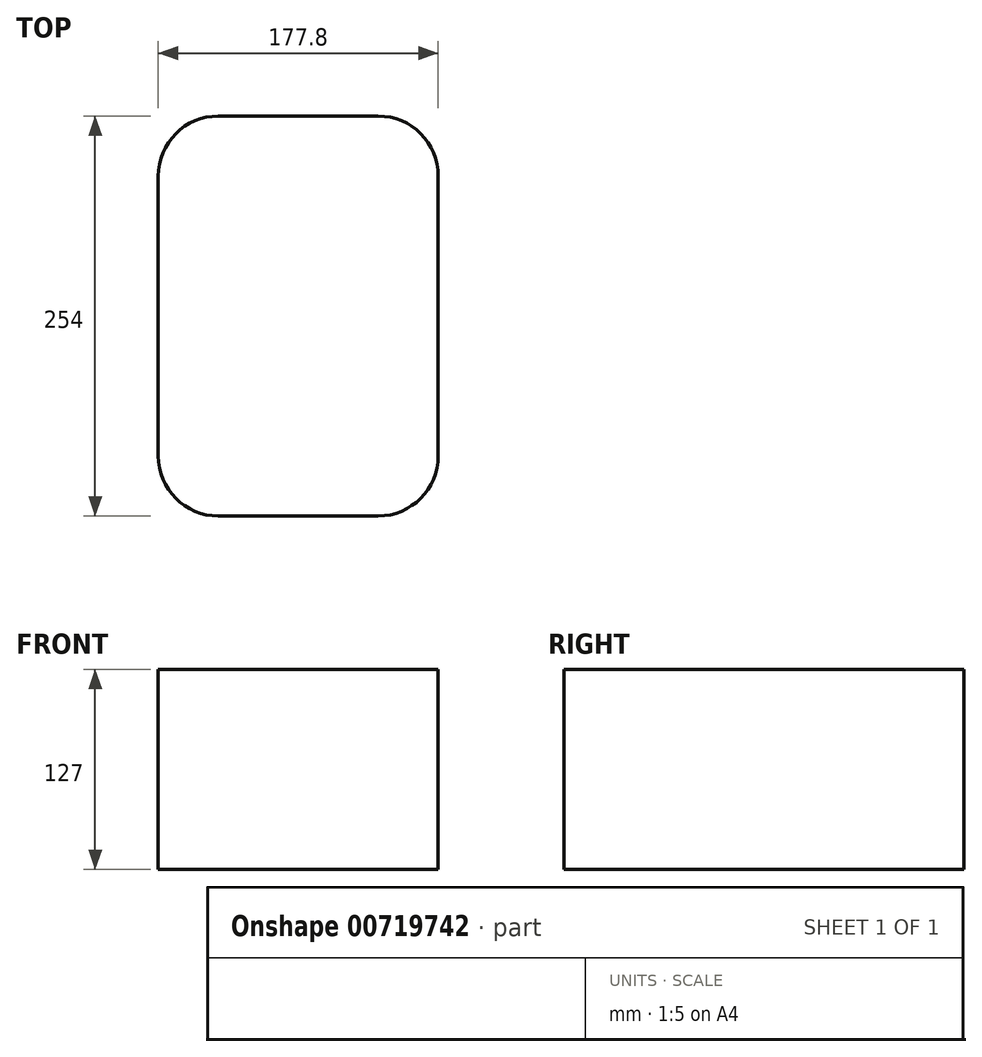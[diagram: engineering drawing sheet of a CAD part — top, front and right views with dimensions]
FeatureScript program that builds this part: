
annotation { "Feature Type Name" : "Feature", "Feature Type Description" : "" }
export const myFeature = defineFeature(function(context is Context, id is Id, definition is map)
    precondition{}
    {
        {
            var Q0;
            Q0=qCreatedBy(makeId("Front.planeOp"),FACE);
            var sketch = newSketch(context, id + "F0", { "sketchPlane" : qUnion([Q0])});
            skLineSegment(sketch, "E0.bottom", {"start": v(0, 127) * mm, "end": v(177.8, 127) * mm});
            skLineSegment(sketch, "E0.top", {"start": v(0, 0) * mm, "end": v(177.8, 0) * mm});
            skLineSegment(sketch, "E0.left", {"start": v(0, 127) * mm, "end": v(0, 0) * mm});
            skLineSegment(sketch, "E0.right", {"start": v(177.8, 127) * mm, "end": v(177.8, 0) * mm});
            skSolve(sketch);
        }
        {
            var Q0;
            Q0 = qSketchRegion(id + "F0", true);
            extrude(context, id + "F1", {"entities" : qUnion([Q0]), "depth" : 254 * mm, "offsetDistance" : 25.4 * mm});
        }
        {
            var Q0;
            Q0=makeQuery(id+"F1.opExtrude","CAP_EDGE",EDGE,{"disambiguationData":[OSD([sQuery(id+"F0.wireOp",EDGE,"E0.left")])],"isStart":false});
            var Q1;
            Q1=makeQuery(id+"F1.opExtrude","CAP_EDGE",EDGE,{"disambiguationData":[OSD([sQuery(id+"F0.wireOp",EDGE,"E0.right")])],"isStart":false});
            var Q2;
            Q2=makeQuery(id+"F1.opExtrude","CAP_EDGE",EDGE,{"disambiguationData":[OSD([sQuery(id+"F0.wireOp",EDGE,"E0.right")])],"isStart":true});
            var Q3;
            Q3=makeQuery(id+"F1.opExtrude","CAP_EDGE",EDGE,{"disambiguationData":[OSD([sQuery(id+"F0.wireOp",EDGE,"E0.left")])],"isStart":true});
            fillet(context, id + "F2", {"entities" : qUnion([Q0, Q1, Q2, Q3]), "radius" : 38.1 * mm, "tangentPropagation" : true, "allowEdgeOverflow" : false});
        }
    });
